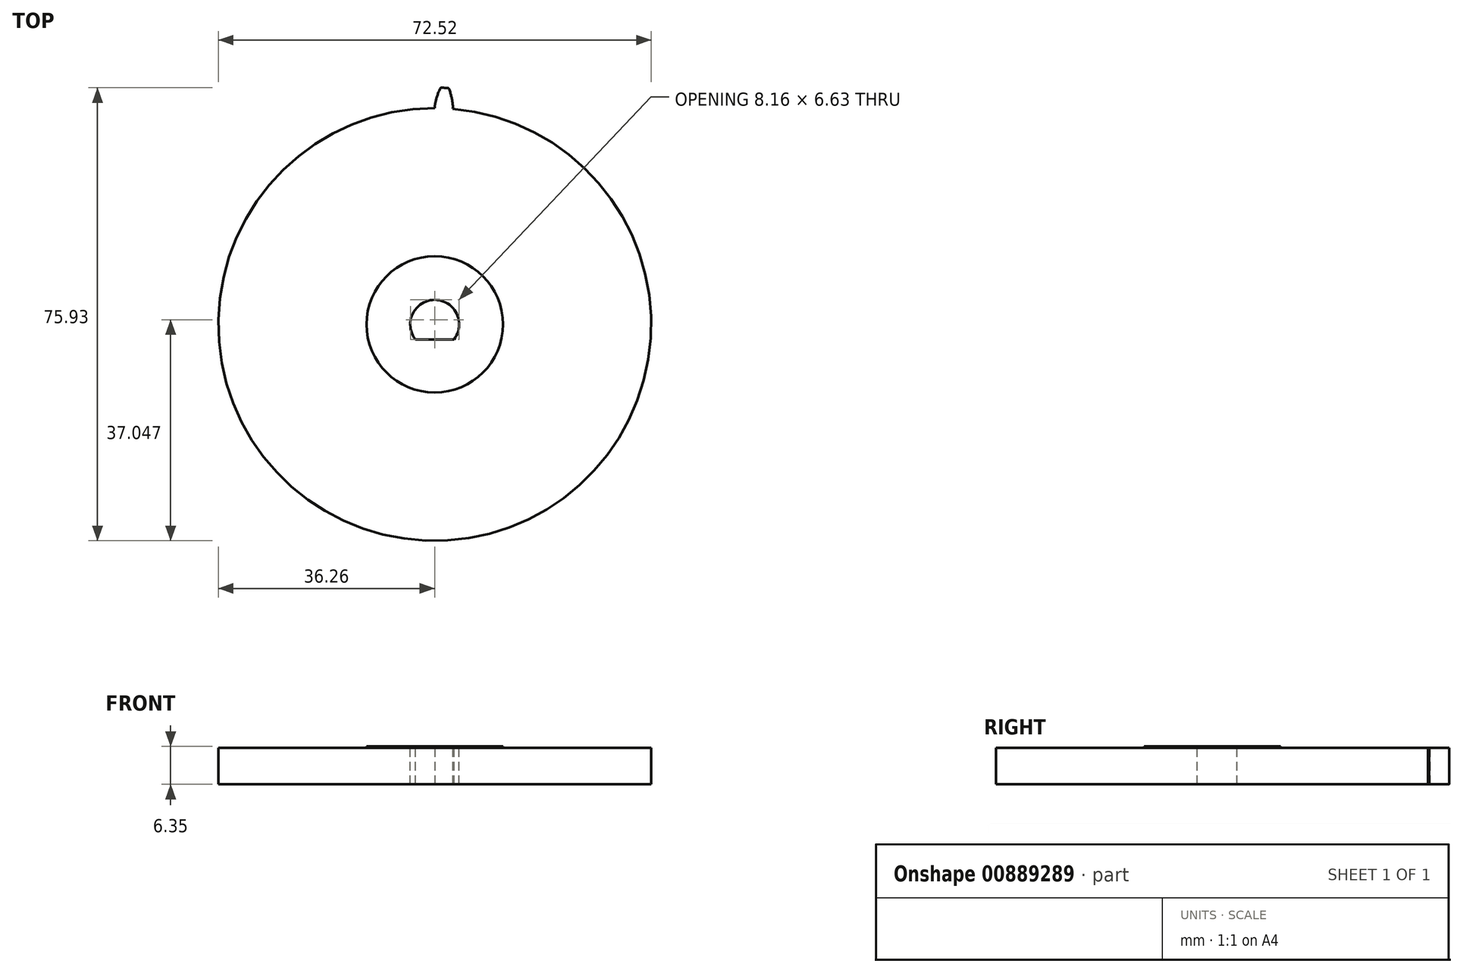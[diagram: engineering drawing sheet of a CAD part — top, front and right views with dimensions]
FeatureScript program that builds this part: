
annotation { "Feature Type Name" : "Feature", "Feature Type Description" : "" }
export const myFeature = defineFeature(function(context is Context, id is Id, definition is map)
    precondition{}
    {
        {
            assignVariable(context, id + "F0", {"name" : "N", "anyValue" : 16 * 3});
        }
        {
            var Q0;
            Q0=qCreatedBy(makeId("Top.planeOp"),FACE);
            var sketch = newSketch(context, id + "F1", { "sketchPlane" : qUnion([Q0])});
            skCircle(sketch, "E0", {"center": v(0, 0) * mm, "radius": 36.44 * mm, "construction": true});
            skCircle(sketch, "E1", {"center": v(0, 0) * mm, "radius": 38.1 * mm, "construction": true});
            skCircle(sketch, "E2", {"center": v(0, 0) * mm, "radius": 39.69 * mm});
            skLineSegment(sketch, "E3", {"start": v(0, 0) * mm, "end": v(0, 36.44) * mm, "construction": true});
            skLineSegment(sketch, "E4", {"start": v(0, 0) * mm, "end": v(2.38, 36.36) * mm, "construction": true});
            skLineSegment(sketch, "E5", {"start": v(0, 0) * mm, "end": v(4.76, 36.12) * mm, "construction": true});
            skLineSegment(sketch, "E6", {"start": v(0, 0) * mm, "end": v(7.1, 35.74) * mm, "construction": true});
            skLineSegment(sketch, "E7", {"start": v(0, 0) * mm, "end": v(9.43, 35.2) * mm, "construction": true});
            skCircle(sketch, "E8", {"center": v(0, 0) * mm, "radius": 36.26 * mm});
            skLineSegment(sketch, "E9", {"start": v(2.38, 36.36) * mm, "end": v(0, 36.51) * mm, "construction": true});
            skLineSegment(sketch, "E10", {"start": v(4.76, 36.12) * mm, "end": v(0.03, 36.75) * mm, "construction": true});
            skLineSegment(sketch, "E11", {"start": v(7.1, 35.74) * mm, "end": v(0.1, 37.13) * mm, "construction": true});
            skLineSegment(sketch, "E12", {"start": v(9.43, 35.2) * mm, "end": v(0.22, 37.66) * mm, "construction": true});
            skLineSegment(sketch, "E13", {"start": v(0, 0) * mm, "end": v(11.71, 34.5) * mm, "construction": true});
            skLineSegment(sketch, "E14", {"start": v(11.71, 34.5) * mm, "end": v(0.42, 38.33) * mm, "construction": true});
            skLineSegment(sketch, "E15", {"start": v(0, 0) * mm, "end": v(13.94, 33.66) * mm, "construction": true});
            skLineSegment(sketch, "E16", {"start": v(0, 0) * mm, "end": v(16.11, 32.68) * mm, "construction": true});
            skLineSegment(sketch, "E17", {"start": v(0, 0) * mm, "end": v(18.22, 31.55) * mm, "construction": true});
            skLineSegment(sketch, "E18", {"start": v(13.94, 33.66) * mm, "end": v(0.72, 39.14) * mm, "construction": true});
            skLineSegment(sketch, "E19", {"start": v(16.11, 32.68) * mm, "end": v(1.14, 40.06) * mm, "construction": true});
            skLineSegment(sketch, "E20", {"start": v(18.22, 31.55) * mm, "end": v(1.7, 41.1) * mm, "construction": true});
            skLineSegment(sketch, "E21", {"start": v(0, 0) * mm, "end": v(20.24, 30.3) * mm, "construction": true});
            skLineSegment(sketch, "E22", {"start": v(0, 0) * mm, "end": v(22.18, 28.9) * mm, "construction": true});
            skLineSegment(sketch, "E23", {"start": v(0, 0) * mm, "end": v(24.02, 27.4) * mm, "construction": true});
            skLineSegment(sketch, "E24", {"start": v(0, 0) * mm, "end": v(25.76, 25.76) * mm, "construction": true});
            skLineSegment(sketch, "E25", {"start": v(0, 0) * mm, "end": v(27.4, 24.02) * mm, "construction": true});
            skLineSegment(sketch, "E26", {"start": v(20.24, 30.3) * mm, "end": v(2.4, 42.22) * mm, "construction": true});
            skLineSegment(sketch, "E27", {"start": v(22.18, 28.9) * mm, "end": v(3.26, 43.42) * mm, "construction": true});
            skLineSegment(sketch, "E28", {"start": v(24.02, 27.4) * mm, "end": v(4.3, 44.69) * mm, "construction": true});
            skLineSegment(sketch, "E29", {"start": v(25.76, 25.76) * mm, "end": v(5.53, 46) * mm, "construction": true});
            skLineSegment(sketch, "E30", {"start": v(27.4, 24.02) * mm, "end": v(6.95, 47.33) * mm, "construction": true});
            skLineSegment(sketch, "E31", {"start": v(0, 0) * mm, "end": v(28.9, 22.18) * mm, "construction": true});
            skLineSegment(sketch, "E32", {"start": v(28.9, 22.18) * mm, "end": v(8.58, 48.67) * mm, "construction": true});
            skLineSegment(sketch, "E33", {"start": v(0, 0) * mm, "end": v(30.3, 20.24) * mm, "construction": true});
            skLineSegment(sketch, "E34", {"start": v(30.3, 20.24) * mm, "end": v(10.42, 49.98) * mm, "construction": true});
            skSolve(sketch);
        }
        {
            var Q0;
            Q0=qCreatedBy(makeId("Top.planeOp"),FACE);
            var sketch = newSketch(context, id + "F2", { "sketchPlane" : qUnion([Q0])});
            skLineSegment(sketch, "E35.0", {"start": v(28.9, 22.18) * mm, "end": v(8.58, 48.67) * mm, "construction": true});
            skLineSegment(sketch, "E35.1", {"start": v(27.4, 24.02) * mm, "end": v(6.95, 47.33) * mm, "construction": true});
            skLineSegment(sketch, "E35.2", {"start": v(25.76, 25.76) * mm, "end": v(5.53, 46) * mm, "construction": true});
            skLineSegment(sketch, "E35.3", {"start": v(24.02, 27.4) * mm, "end": v(4.3, 44.69) * mm, "construction": true});
            skLineSegment(sketch, "E35.4", {"start": v(22.18, 28.9) * mm, "end": v(3.26, 43.42) * mm, "construction": true});
            skLineSegment(sketch, "E35.5", {"start": v(20.24, 30.3) * mm, "end": v(2.4, 42.22) * mm, "construction": true});
            skLineSegment(sketch, "E35.6", {"start": v(18.22, 31.55) * mm, "end": v(1.7, 41.1) * mm, "construction": true});
            skLineSegment(sketch, "E35.7", {"start": v(16.11, 32.68) * mm, "end": v(1.14, 40.06) * mm, "construction": true});
            skLineSegment(sketch, "E35.8", {"start": v(13.94, 33.66) * mm, "end": v(0.72, 39.14) * mm, "construction": true});
            skLineSegment(sketch, "E35.9", {"start": v(11.71, 34.5) * mm, "end": v(0.42, 38.33) * mm, "construction": true});
            skLineSegment(sketch, "E35.10", {"start": v(9.43, 35.2) * mm, "end": v(0.22, 37.66) * mm, "construction": true});
            skLineSegment(sketch, "E35.11", {"start": v(7.1, 35.74) * mm, "end": v(0.1, 37.13) * mm, "construction": true});
            skLineSegment(sketch, "E35.12", {"start": v(4.76, 36.12) * mm, "end": v(0.03, 36.75) * mm, "construction": true});
            skLineSegment(sketch, "E35.13", {"start": v(2.38, 36.36) * mm, "end": v(0, 36.51) * mm, "construction": true});
            skCircle(sketch, "E35.14", {"center": v(0, 0) * mm, "radius": 36.44 * mm});
            skCircle(sketch, "E35.15", {"center": v(0, 0) * mm, "radius": 36.26 * mm});
            skCircle(sketch, "E35.16", {"center": v(0, 0) * mm, "radius": 38.1 * mm, "construction": true});
            skCircle(sketch, "E35.17", {"center": v(0, 0) * mm, "radius": 39.69 * mm});
            skLineSegment(sketch, "E36.0", {"start": v(30.3, 20.24) * mm, "end": v(10.42, 49.98) * mm, "construction": true});
            skLineSegment(sketch, "E37.0", {"start": v(0, 0) * mm, "end": v(0, 36.44) * mm, "construction": true});
            skFitSpline(sketch, "E38", {"points": [v(0, 36.44) * mm, v(0, 36.51) * mm, v(0.03, 36.75) * mm, v(0.1, 37.13) * mm, v(0.22, 37.66) * mm, v(0.42, 38.33) * mm, v(0.72, 39.14) * mm, v(1.14, 40.06) * mm, v(1.7, 41.1) * mm, v(2.4, 42.22) * mm, v(3.26, 43.42) * mm, v(4.3, 44.69) * mm, v(5.53, 46) * mm, v(6.95, 47.33) * mm, v(8.58, 48.67) * mm, v(10.42, 49.98) * mm, v(0, 0) * mm], "startDerivative": vector(0.82, 18.8) * mm, "endDerivative": vector(-98.3, -471.48) * mm});
            skLineSegment(sketch, "E39", {"start": v(0.34, 38.1) * mm, "end": v(0, 0) * mm, "construction": true});
            skLineSegment(sketch, "E40", {"start": v(0, 0) * mm, "end": v(1.66, 39.65) * mm, "construction": true});
            skFitSpline(sketch, "E41.MirrorCS", {"points": [v(3.04, 36.3) * mm, v(3.04, 36.39) * mm, v(3.04, 36.62) * mm, v(3, 37) * mm, v(2.93, 37.55) * mm, v(2.78, 38.24) * mm, v(2.54, 39.06) * mm, v(2.2, 40.02) * mm, v(1.74, 41.1) * mm, v(1.13, 42.27) * mm, v(0.37, 43.54) * mm, v(-0.56, 44.9) * mm, v(-1.67, 46.3) * mm, v(-2.98, 47.75) * mm, v(-4.5, 49.21) * mm, v(-6.22, 50.68) * mm, v(0, 0) * mm], "startDerivative": vector(0.75, 18.81) * mm, "endDerivative": vector(58.64, -478.03) * mm});
            skLineSegment(sketch, "E42", {"start": v(3.04, 36.3) * mm, "end": v(3.02, 36.14) * mm});
            skLineSegment(sketch, "E43", {"start": v(0, 36.44) * mm, "end": v(0, 36.26) * mm});
            skSolve(sketch);
        }
        {
            var Q0;
            {var subQ3=sQuery(id+"F2.wireOp",EDGE,"E41.MirrorCS");var subQ6=sQuery(id+"F2.wireOp",EDGE,"E35.17");var subQ8=makeQuery(id+"F2.imprint","INTERSECT",VERTEX,{"disambiguationData":[OD(1.0)],"derivedFrom":[subQ6,subQ3]});Q0=makeQuery(id+"F2.imprint","IMPRINT",FACE,{"disambiguationData":[TD([[makeQuery(id+"F2.imprint","IMPRINT",EDGE,{"disambiguationData":[TD([[subQ8,-1.0]])],"derivedFrom":subQ6}),1.0]])]});}
            var Q1;
            {var subQ3=sQuery(id+"F2.wireOp",EDGE,"E41.MirrorCS");var subQ5=sQuery(id+"F2.wireOp",EDGE,"E35.15");var subQ6=makeQuery(id+"F2.imprint","INTERSECT",VERTEX,{"derivedFrom":[subQ5,subQ3]});Q1=makeQuery(id+"F2.imprint","IMPRINT",FACE,{"disambiguationData":[TD([[makeQuery(id+"F2.imprint","IMPRINT",EDGE,{"disambiguationData":[TD([[subQ6,-1.0]])],"derivedFrom":subQ5}),1.0]])]});}
            var Q2;
            {var subQ2=sQuery(id+"F2.wireOp",EDGE,"E42");Q2=makeQuery(id+"F2.imprint","IMPRINT",FACE,{"disambiguationData":[TD([[makeQuery(id+"F2.imprint","IMPRINT",EDGE,{"derivedFrom":subQ2}),-1.0]])]});}
            extrude(context, id + "F3", {"entities" : qUnion([Q0, Q1, Q2]), "depth" : 6.35 * mm, "offsetDistance" : 25.4 * mm});
        }
        {
            var Q0;
            Q0=makeQuery(id+"F3.opExtrude","SWEPT_EDGE",EDGE,{"disambiguationData":[OSD([sQuery(id+"F2.wireOp",EDGE,"E35.17"),sQuery(id+"F2.wireOp",EDGE,"E38")])]});
            var Q1;
            Q1=makeQuery(id+"F3.opExtrude","SWEPT_EDGE",EDGE,{"disambiguationData":[OSD([sQuery(id+"F2.wireOp",EDGE,"E35.17"),sQuery(id+"F2.wireOp",EDGE,"E41.MirrorCS")])]});
            fillet(context, id + "F4", {"entities" : qUnion([Q0, Q1]), "radius" : 0.25 * mm, "tangentPropagation" : true, "allowEdgeOverflow" : false});
        }
        {
            var Q0;
            Q0=qCreatedBy(makeId("Right.planeOp"),FACE);
            var sketch = newSketch(context, id + "F5", { "sketchPlane" : qUnion([Q0])});
            skLineSegment(sketch, "E44", {"start": v(0, 0) * mm, "end": v(0, 43.3) * mm, "construction": true});
            skSolve(sketch);
        }
        {
            var Q0;
            Q0=makeQuery(id+"F3.opExtrude","SWEPT_BODY",BODY,{"disambiguationData":[OSD([sQuery(id+"F2.wireOp",EDGE,"E35.15"),sQuery(id+"F2.wireOp",EDGE,"E35.17"),sQuery(id+"F2.wireOp",EDGE,"E38"),sQuery(id+"F2.wireOp",EDGE,"E41.MirrorCS"),sQuery(id+"F2.wireOp",EDGE,"9305e2c8-a00a-4cbc-a3b2-8fc88bc1717c"),sQuery(id+"F2.wireOp",EDGE,"f762f43d-eaf9-45ff-b6cd-062fd530227c")])]});
            var Q1;
            Q1=sQuery(id+"F5.wireOp",EDGE,"E44");
            circularPattern(context, id + "F6", {"operationType" : NewBodyOperationType.ADD, "entities" : qUnion([Q0]), "axis" : qUnion([Q1]), "angle" : (360 / getVariable(context, 'N')) * degree, "instanceCount" : getVariable(context, 'N'), "oppositeDirection" : true});
        }
        {
            var Q0;
            {var subQ0=makeQuery(id+"F3.opExtrude","CAP_FACE",FACE,{"disambiguationData":[OSD([sQuery(id+"F2.wireOp",EDGE,"E35.15"),sQuery(id+"F2.wireOp",EDGE,"E35.17"),sQuery(id+"F2.wireOp",EDGE,"E38"),sQuery(id+"F2.wireOp",EDGE,"E41.MirrorCS"),sQuery(id+"F2.wireOp",EDGE,"E42"),sQuery(id+"F2.wireOp",EDGE,"E43")])],"isStart":false});Q0=makeQuery(id+"F6.boolean.opBoolean","MERGE",FACE,{"derivedFrom":[subQ0,makeQuery(id+"F6.opPattern","COPY",FACE,{"derivedFrom":subQ0,"instanceName":"1"}),makeQuery(id+"F6.opPattern","COPY",FACE,{"derivedFrom":subQ0,"instanceName":"2"}),makeQuery(id+"F6.opPattern","COPY",FACE,{"derivedFrom":subQ0,"instanceName":"3"}),makeQuery(id+"F6.opPattern","COPY",FACE,{"derivedFrom":subQ0,"instanceName":"4"}),makeQuery(id+"F6.opPattern","COPY",FACE,{"derivedFrom":subQ0,"instanceName":"5"}),makeQuery(id+"F6.opPattern","COPY",FACE,{"derivedFrom":subQ0,"instanceName":"6"}),makeQuery(id+"F6.opPattern","COPY",FACE,{"derivedFrom":subQ0,"instanceName":"7"}),makeQuery(id+"F6.opPattern","COPY",FACE,{"derivedFrom":subQ0,"instanceName":"8"}),makeQuery(id+"F6.opPattern","COPY",FACE,{"derivedFrom":subQ0,"instanceName":"9"}),makeQuery(id+"F6.opPattern","COPY",FACE,{"derivedFrom":subQ0,"instanceName":"10"}),makeQuery(id+"F6.opPattern","COPY",FACE,{"derivedFrom":subQ0,"instanceName":"11"}),makeQuery(id+"F6.opPattern","COPY",FACE,{"derivedFrom":subQ0,"instanceName":"12"}),makeQuery(id+"F6.opPattern","COPY",FACE,{"derivedFrom":subQ0,"instanceName":"13"}),makeQuery(id+"F6.opPattern","COPY",FACE,{"derivedFrom":subQ0,"instanceName":"14"}),makeQuery(id+"F6.opPattern","COPY",FACE,{"derivedFrom":subQ0,"instanceName":"15"}),makeQuery(id+"F6.opPattern","COPY",FACE,{"derivedFrom":subQ0,"instanceName":"16"}),makeQuery(id+"F6.opPattern","COPY",FACE,{"derivedFrom":subQ0,"instanceName":"17"}),makeQuery(id+"F6.opPattern","COPY",FACE,{"derivedFrom":subQ0,"instanceName":"18"}),makeQuery(id+"F6.opPattern","COPY",FACE,{"derivedFrom":subQ0,"instanceName":"19"}),makeQuery(id+"F6.opPattern","COPY",FACE,{"derivedFrom":subQ0,"instanceName":"20"}),makeQuery(id+"F6.opPattern","COPY",FACE,{"derivedFrom":subQ0,"instanceName":"21"}),makeQuery(id+"F6.opPattern","COPY",FACE,{"derivedFrom":subQ0,"instanceName":"22"}),makeQuery(id+"F6.opPattern","COPY",FACE,{"derivedFrom":subQ0,"instanceName":"23"}),makeQuery(id+"F6.opPattern","COPY",FACE,{"derivedFrom":subQ0,"instanceName":"24"}),makeQuery(id+"F6.opPattern","COPY",FACE,{"derivedFrom":subQ0,"instanceName":"25"}),makeQuery(id+"F6.opPattern","COPY",FACE,{"derivedFrom":subQ0,"instanceName":"26"}),makeQuery(id+"F6.opPattern","COPY",FACE,{"derivedFrom":subQ0,"instanceName":"27"}),makeQuery(id+"F6.opPattern","COPY",FACE,{"derivedFrom":subQ0,"instanceName":"28"}),makeQuery(id+"F6.opPattern","COPY",FACE,{"derivedFrom":subQ0,"instanceName":"29"}),makeQuery(id+"F6.opPattern","COPY",FACE,{"derivedFrom":subQ0,"instanceName":"30"}),makeQuery(id+"F6.opPattern","COPY",FACE,{"derivedFrom":subQ0,"instanceName":"31"}),makeQuery(id+"F6.opPattern","COPY",FACE,{"derivedFrom":subQ0,"instanceName":"32"}),makeQuery(id+"F6.opPattern","COPY",FACE,{"derivedFrom":subQ0,"instanceName":"33"}),makeQuery(id+"F6.opPattern","COPY",FACE,{"derivedFrom":subQ0,"instanceName":"34"}),makeQuery(id+"F6.opPattern","COPY",FACE,{"derivedFrom":subQ0,"instanceName":"35"}),makeQuery(id+"F6.opPattern","COPY",FACE,{"derivedFrom":subQ0,"instanceName":"36"}),makeQuery(id+"F6.opPattern","COPY",FACE,{"derivedFrom":subQ0,"instanceName":"37"}),makeQuery(id+"F6.opPattern","COPY",FACE,{"derivedFrom":subQ0,"instanceName":"38"}),makeQuery(id+"F6.opPattern","COPY",FACE,{"derivedFrom":subQ0,"instanceName":"39"}),makeQuery(id+"F6.opPattern","COPY",FACE,{"derivedFrom":subQ0,"instanceName":"40"}),makeQuery(id+"F6.opPattern","COPY",FACE,{"derivedFrom":subQ0,"instanceName":"41"}),makeQuery(id+"F6.opPattern","COPY",FACE,{"derivedFrom":subQ0,"instanceName":"42"}),makeQuery(id+"F6.opPattern","COPY",FACE,{"derivedFrom":subQ0,"instanceName":"43"}),makeQuery(id+"F6.opPattern","COPY",FACE,{"derivedFrom":subQ0,"instanceName":"44"}),makeQuery(id+"F6.opPattern","COPY",FACE,{"derivedFrom":subQ0,"instanceName":"45"}),makeQuery(id+"F6.opPattern","COPY",FACE,{"derivedFrom":subQ0,"instanceName":"46"}),makeQuery(id+"F6.opPattern","COPY",FACE,{"derivedFrom":subQ0,"instanceName":"47"})]});}
            var sketch = newSketch(context, id + "F7", { "sketchPlane" : qUnion([Q0])});
            skCircle(sketch, "E45", {"center": v(0, 0) * mm, "radius": 4.1 * mm});
            skLineSegment(sketch, "E46", {"start": v(-3.23, -2.53) * mm, "end": v(3.23, -2.53) * mm});
            skSolve(sketch);
        }
        {
            var Q0;
            {var subQ0=sQuery(id+"F7.wireOp",EDGE,"E46");Q0=makeQuery(id+"F7.imprint","IMPRINT",FACE,{"disambiguationData":[TD([[makeQuery(id+"F7.imprint","IMPRINT",EDGE,{"derivedFrom":subQ0}),1.0]])]});}
            extrude(context, id + "F8", {"entities" : qUnion([Q0]), "operationType" : NewBodyOperationType.REMOVE, "oppositeDirection" : true, "depth" : 25.4 * mm, "offsetDistance" : 25.4 * mm});
        }
        {
            var Q0;
            {var subQ0=makeQuery(id+"F3.opExtrude","CAP_FACE",FACE,{"disambiguationData":[OSD([sQuery(id+"F2.wireOp",EDGE,"E35.15"),sQuery(id+"F2.wireOp",EDGE,"E35.17"),sQuery(id+"F2.wireOp",EDGE,"E38"),sQuery(id+"F2.wireOp",EDGE,"E41.MirrorCS"),sQuery(id+"F2.wireOp",EDGE,"E42"),sQuery(id+"F2.wireOp",EDGE,"E43")])],"isStart":false});Q0=makeQuery(id+"F6.boolean.opBoolean","MERGE",FACE,{"derivedFrom":[subQ0,makeQuery(id+"F6.opPattern","COPY",FACE,{"derivedFrom":subQ0,"instanceName":"1"}),makeQuery(id+"F6.opPattern","COPY",FACE,{"derivedFrom":subQ0,"instanceName":"2"}),makeQuery(id+"F6.opPattern","COPY",FACE,{"derivedFrom":subQ0,"instanceName":"3"}),makeQuery(id+"F6.opPattern","COPY",FACE,{"derivedFrom":subQ0,"instanceName":"4"}),makeQuery(id+"F6.opPattern","COPY",FACE,{"derivedFrom":subQ0,"instanceName":"5"}),makeQuery(id+"F6.opPattern","COPY",FACE,{"derivedFrom":subQ0,"instanceName":"6"}),makeQuery(id+"F6.opPattern","COPY",FACE,{"derivedFrom":subQ0,"instanceName":"7"}),makeQuery(id+"F6.opPattern","COPY",FACE,{"derivedFrom":subQ0,"instanceName":"8"}),makeQuery(id+"F6.opPattern","COPY",FACE,{"derivedFrom":subQ0,"instanceName":"9"}),makeQuery(id+"F6.opPattern","COPY",FACE,{"derivedFrom":subQ0,"instanceName":"10"}),makeQuery(id+"F6.opPattern","COPY",FACE,{"derivedFrom":subQ0,"instanceName":"11"}),makeQuery(id+"F6.opPattern","COPY",FACE,{"derivedFrom":subQ0,"instanceName":"12"}),makeQuery(id+"F6.opPattern","COPY",FACE,{"derivedFrom":subQ0,"instanceName":"13"}),makeQuery(id+"F6.opPattern","COPY",FACE,{"derivedFrom":subQ0,"instanceName":"14"}),makeQuery(id+"F6.opPattern","COPY",FACE,{"derivedFrom":subQ0,"instanceName":"15"}),makeQuery(id+"F6.opPattern","COPY",FACE,{"derivedFrom":subQ0,"instanceName":"16"}),makeQuery(id+"F6.opPattern","COPY",FACE,{"derivedFrom":subQ0,"instanceName":"17"}),makeQuery(id+"F6.opPattern","COPY",FACE,{"derivedFrom":subQ0,"instanceName":"18"}),makeQuery(id+"F6.opPattern","COPY",FACE,{"derivedFrom":subQ0,"instanceName":"19"}),makeQuery(id+"F6.opPattern","COPY",FACE,{"derivedFrom":subQ0,"instanceName":"20"}),makeQuery(id+"F6.opPattern","COPY",FACE,{"derivedFrom":subQ0,"instanceName":"21"}),makeQuery(id+"F6.opPattern","COPY",FACE,{"derivedFrom":subQ0,"instanceName":"22"}),makeQuery(id+"F6.opPattern","COPY",FACE,{"derivedFrom":subQ0,"instanceName":"23"}),makeQuery(id+"F6.opPattern","COPY",FACE,{"derivedFrom":subQ0,"instanceName":"24"}),makeQuery(id+"F6.opPattern","COPY",FACE,{"derivedFrom":subQ0,"instanceName":"25"}),makeQuery(id+"F6.opPattern","COPY",FACE,{"derivedFrom":subQ0,"instanceName":"26"}),makeQuery(id+"F6.opPattern","COPY",FACE,{"derivedFrom":subQ0,"instanceName":"27"}),makeQuery(id+"F6.opPattern","COPY",FACE,{"derivedFrom":subQ0,"instanceName":"28"}),makeQuery(id+"F6.opPattern","COPY",FACE,{"derivedFrom":subQ0,"instanceName":"29"}),makeQuery(id+"F6.opPattern","COPY",FACE,{"derivedFrom":subQ0,"instanceName":"30"}),makeQuery(id+"F6.opPattern","COPY",FACE,{"derivedFrom":subQ0,"instanceName":"31"}),makeQuery(id+"F6.opPattern","COPY",FACE,{"derivedFrom":subQ0,"instanceName":"32"}),makeQuery(id+"F6.opPattern","COPY",FACE,{"derivedFrom":subQ0,"instanceName":"33"}),makeQuery(id+"F6.opPattern","COPY",FACE,{"derivedFrom":subQ0,"instanceName":"34"}),makeQuery(id+"F6.opPattern","COPY",FACE,{"derivedFrom":subQ0,"instanceName":"35"}),makeQuery(id+"F6.opPattern","COPY",FACE,{"derivedFrom":subQ0,"instanceName":"36"}),makeQuery(id+"F6.opPattern","COPY",FACE,{"derivedFrom":subQ0,"instanceName":"37"}),makeQuery(id+"F6.opPattern","COPY",FACE,{"derivedFrom":subQ0,"instanceName":"38"}),makeQuery(id+"F6.opPattern","COPY",FACE,{"derivedFrom":subQ0,"instanceName":"39"}),makeQuery(id+"F6.opPattern","COPY",FACE,{"derivedFrom":subQ0,"instanceName":"40"}),makeQuery(id+"F6.opPattern","COPY",FACE,{"derivedFrom":subQ0,"instanceName":"41"}),makeQuery(id+"F6.opPattern","COPY",FACE,{"derivedFrom":subQ0,"instanceName":"42"}),makeQuery(id+"F6.opPattern","COPY",FACE,{"derivedFrom":subQ0,"instanceName":"43"}),makeQuery(id+"F6.opPattern","COPY",FACE,{"derivedFrom":subQ0,"instanceName":"44"}),makeQuery(id+"F6.opPattern","COPY",FACE,{"derivedFrom":subQ0,"instanceName":"45"}),makeQuery(id+"F6.opPattern","COPY",FACE,{"derivedFrom":subQ0,"instanceName":"46"}),makeQuery(id+"F6.opPattern","COPY",FACE,{"derivedFrom":subQ0,"instanceName":"47"})]});}
            var sketch = newSketch(context, id + "F9", { "sketchPlane" : qUnion([Q0])});
            skCircle(sketch, "E47", {"center": v(0, 0) * mm, "radius": 11.43 * mm});
            skSolve(sketch);
        }
        {
            var Q0;
            Q0=makeQuery(id+"F9.imprint","IMPRINT",FACE,{"disambiguationData":[TD([[makeQuery(id+"F9.imprint","IMPRINT",EDGE,{"derivedFrom":sQuery(id+"F9.wireOp",EDGE,"E47")}),-1.0]])]});
            extrude(context, id + "F10", {"entities" : qUnion([Q0]), "operationType" : NewBodyOperationType.REMOVE, "oppositeDirection" : true, "depth" : 0.25 * mm, "offsetDistance" : 25.4 * mm});
        }
    });
